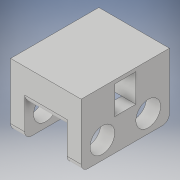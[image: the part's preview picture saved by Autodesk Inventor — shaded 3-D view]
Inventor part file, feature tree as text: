
AUTODESK INVENTOR PART (.ipt)
format: ipt  version: 2019 (Build 230136000, 136)  size: 152,576 bytes
history: native  units: mm
features: sketch x3, extrude x2, hole x1, plane x1, mirror x1, fillet x1
ambient origin geometry x8: Origin, YZ Plane, XZ Plane, XY Plane, X Axis, Y Axis, Z Axis, Center Point
bodies: Solid1 (feature_tree)
feature tree (9):
  extrude  "Extrusion1"  Depth=20.0mm
  hole  "Hole1"  [1 undecoded]
  plane  "Work Plane1"
  mirror  "Mirror1"
  fillet  "Fillet1"  Radius=5.0mm
  extrude  "Extrusion2"  Depth=4.0mm
  sketch  "Sketch1"  dims[d0=18.0mm d1=20.0mm]
  sketch  "Sketch2"  dims[d2=9.0mm d6=25.0mm d7=0.0mm d10=5.0mm]
  sketch  "Sketch3"  dims[d11=6.0mm d12=7.0mm d13=6.0mm d14=4.0mm d15=2.0mm d16=90.0deg d17=8.0mm d18=20.594885mm d19=12.5mm d20=2.0mm d21=6.0mm d22=8.0mm d24=9.0mm d25=9.5mm d26=20.0mm d27=0.0mm d28=12.0mm d29=4.0mm d30=4.0mm]
note: 1 required parameter value undecoded (feature->parameter linkage not recoverable at this tier; creation-order binding heuristic only, values carry confidence <= 0.55)
